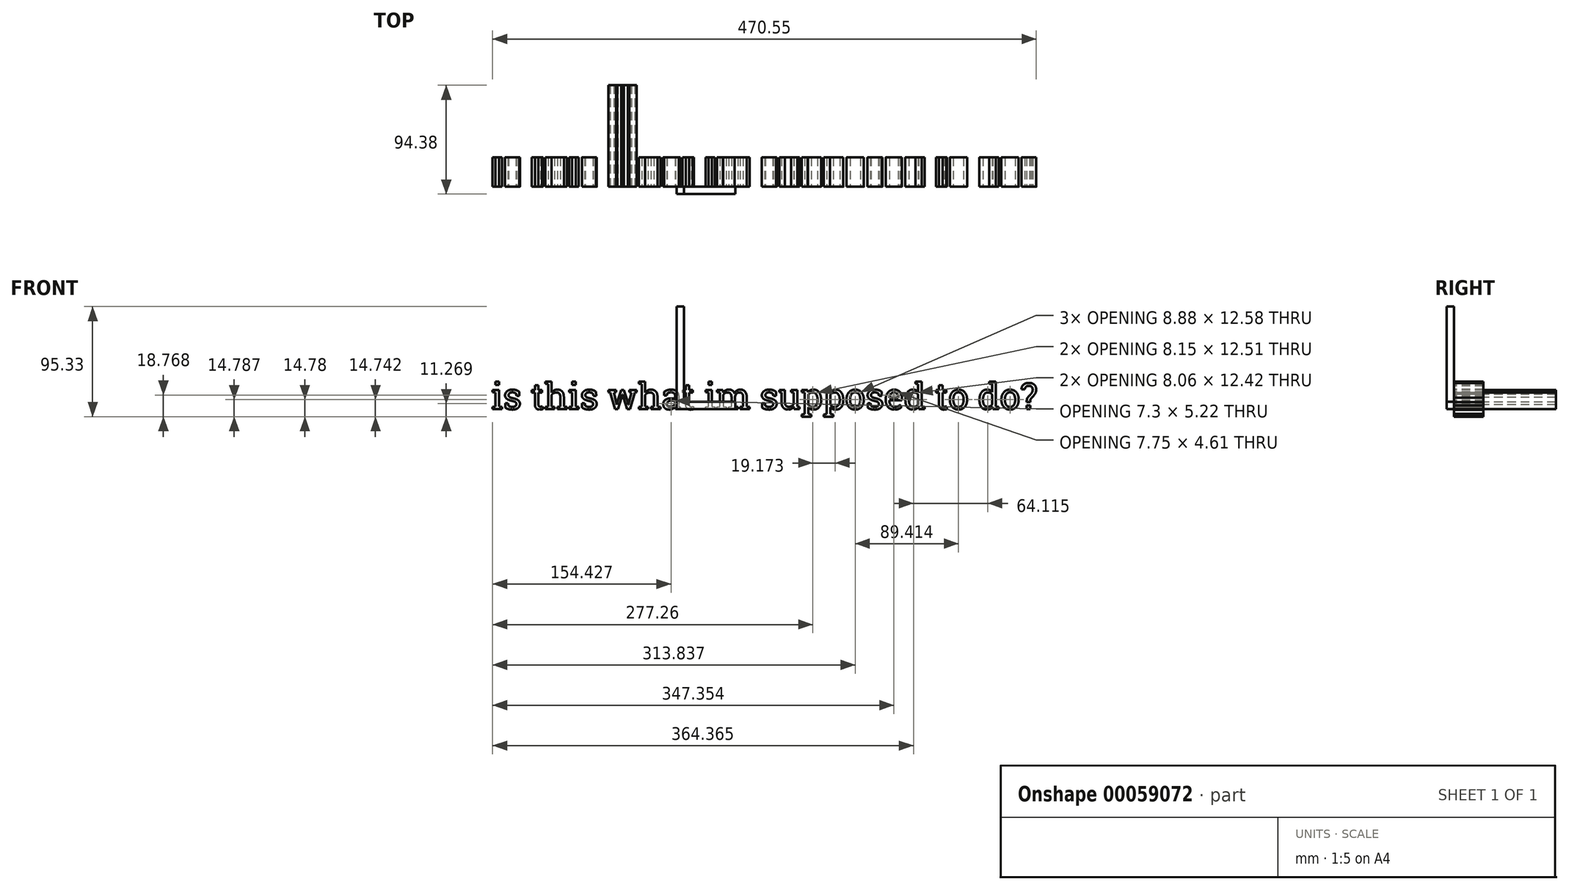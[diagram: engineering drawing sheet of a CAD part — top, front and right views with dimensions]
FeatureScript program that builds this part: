
annotation { "Feature Type Name" : "Feature", "Feature Type Description" : "" }
export const myFeature = defineFeature(function(context is Context, id is Id, definition is map)
    precondition{}
    {
        {
            var Q0;
            Q0=qCreatedBy(makeId("Front.planeOp"),FACE);
            var sketch = newSketch(context, id + "F0", { "sketchPlane" : qUnion([Q0])});
            skLineSegment(sketch, "E0", {"start": v(0, 88.9) * mm, "end": v(0, 0) * mm});
            skLineSegment(sketch, "E1", {"start": v(0, 0) * mm, "end": v(50.8, 0) * mm});
            skLineSegment(sketch, "E2", {"start": v(50.8, 0) * mm, "end": v(50.8, 6.35) * mm});
            skLineSegment(sketch, "E3", {"start": v(50.8, 6.35) * mm, "end": v(6.35, 6.35) * mm});
            skLineSegment(sketch, "E4", {"start": v(6.35, 6.35) * mm, "end": v(6.35, 88.9) * mm});
            skLineSegment(sketch, "E5", {"start": v(6.35, 88.9) * mm, "end": v(0, 88.9) * mm});
            skSolve(sketch);
        }
        {
            var Q0;
            Q0=makeQuery(id+"F0.imprint","IMPRINT",FACE,{"disambiguationData":[TD([[makeQuery(id+"F0.imprint","IMPRINT",EDGE,{"derivedFrom":sQuery(id+"F0.wireOp",EDGE,"E0")}),1.0]])]});
            extrude(context, id + "F1", {"entities" : qUnion([Q0]), "depth" : 6.35 * mm});
        }
        {
            var Q0;
            Q0=qCreatedBy(makeId("Front.planeOp"),FACE);
            var sketch = newSketch(context, id + "F2", { "sketchPlane" : qUnion([Q0])});
            skText(sketch, "E6", { "text": "is this what im supposed to do?", "fontName": "RobotoSlab-Regular.ttf"});
            const initialGuessF2  = {"E6": [-0.16075, 0, 1, 0, 0.0228]};
            skSetInitialGuess(sketch, initialGuessF2);
            skSolve(sketch);
        }
        {
            var Q0;
            Q0=makeQuery(id+"F2.imprint","IMPRINT",FACE,{"disambiguationData":[TD([[makeQuery(id+"F2.imprint","IMPRINT",EDGE,{"derivedFrom":sQuery(id+"F2.wireOp",EDGE,"E6.sketch_text.stroke-134")}),-1.0]])]});
            extrude(context, id + "F3", {"entities" : qUnion([Q0]), "oppositeDirection" : true, "depth" : 88.03 * mm});
        }
        {
            var Q0;
            Q0=makeQuery(id+"F2.imprint","IMPRINT",FACE,{"disambiguationData":[TD([[makeQuery(id+"F2.imprint","IMPRINT",EDGE,{"derivedFrom":sQuery(id+"F2.wireOp",EDGE,"E6.sketch_text.stroke-0")}),-1.0]])]});
            var Q1;
            Q1=makeQuery(id+"F2.imprint","IMPRINT",FACE,{"disambiguationData":[TD([[makeQuery(id+"F2.imprint","IMPRINT",EDGE,{"derivedFrom":sQuery(id+"F2.wireOp",EDGE,"E6.sketch_text.stroke-14")}),-1.0]])]});
            var Q2;
            Q2=makeQuery(id+"F2.imprint","IMPRINT",FACE,{"disambiguationData":[TD([[makeQuery(id+"F2.imprint","IMPRINT",EDGE,{"derivedFrom":sQuery(id+"F2.wireOp",EDGE,"E6.sketch_text.stroke-44")}),-1.0]])]});
            var Q3;
            Q3=makeQuery(id+"F2.imprint","IMPRINT",FACE,{"disambiguationData":[TD([[makeQuery(id+"F2.imprint","IMPRINT",EDGE,{"derivedFrom":sQuery(id+"F2.wireOp",EDGE,"E6.sketch_text.stroke-64")}),-1.0]])]});
            var Q4;
            Q4=makeQuery(id+"F2.imprint","IMPRINT",FACE,{"disambiguationData":[TD([[makeQuery(id+"F2.imprint","IMPRINT",EDGE,{"derivedFrom":sQuery(id+"F2.wireOp",EDGE,"E6.sketch_text.stroke-90")}),-1.0]])]});
            var Q5;
            Q5=makeQuery(id+"F2.imprint","IMPRINT",FACE,{"disambiguationData":[TD([[makeQuery(id+"F2.imprint","IMPRINT",EDGE,{"derivedFrom":sQuery(id+"F2.wireOp",EDGE,"E6.sketch_text.stroke-104")}),-1.0]])]});
            var Q6;
            Q6=makeQuery(id+"F2.imprint","IMPRINT",FACE,{"disambiguationData":[TD([[makeQuery(id+"F2.imprint","IMPRINT",EDGE,{"derivedFrom":sQuery(id+"F2.wireOp",EDGE,"E6.sketch_text.stroke-10")}),-1.0]])]});
            var Q7;
            Q7=makeQuery(id+"F2.imprint","IMPRINT",FACE,{"disambiguationData":[TD([[makeQuery(id+"F2.imprint","IMPRINT",EDGE,{"derivedFrom":sQuery(id+"F2.wireOp",EDGE,"E6.sketch_text.stroke-100")}),-1.0]])]});
            var Q8;
            Q8=makeQuery(id+"F2.imprint","IMPRINT",FACE,{"disambiguationData":[TD([[makeQuery(id+"F2.imprint","IMPRINT",EDGE,{"derivedFrom":sQuery(id+"F2.wireOp",EDGE,"E6.sketch_text.stroke-164")}),-1.0]])]});
            var Q9;
            Q9=makeQuery(id+"F2.imprint","IMPRINT",FACE,{"disambiguationData":[TD([[makeQuery(id+"F2.imprint","IMPRINT",EDGE,{"derivedFrom":sQuery(id+"F2.wireOp",EDGE,"E6.sketch_text.stroke-190")}),-1.0]])]});
            extrude(context, id + "F4", {"entities" : qUnion([Q0, Q1, Q2, Q3, Q4, Q5, Q6, Q7, Q8, Q9]), "operationType" : NewBodyOperationType.ADD, "oppositeDirection" : true, "depth" : 25.4 * mm});
        }
        {
            var Q0;
            Q0=makeQuery(id+"F2.imprint","IMPRINT",FACE,{"disambiguationData":[TD([[makeQuery(id+"F2.imprint","IMPRINT",EDGE,{"derivedFrom":sQuery(id+"F2.wireOp",EDGE,"E6.sketch_text.stroke-225")}),-1.0]])]});
            var Q1;
            Q1=makeQuery(id+"F2.imprint","IMPRINT",FACE,{"disambiguationData":[TD([[makeQuery(id+"F2.imprint","IMPRINT",EDGE,{"derivedFrom":sQuery(id+"F2.wireOp",EDGE,"E6.sketch_text.stroke-245")}),-1.0]])]});
            var Q2;
            Q2=makeQuery(id+"F2.imprint","IMPRINT",FACE,{"disambiguationData":[TD([[makeQuery(id+"F2.imprint","IMPRINT",EDGE,{"derivedFrom":sQuery(id+"F2.wireOp",EDGE,"E6.sketch_text.stroke-259")}),-1.0]])]});
            var Q3;
            Q3=makeQuery(id+"F2.imprint","IMPRINT",FACE,{"disambiguationData":[TD([[makeQuery(id+"F2.imprint","IMPRINT",EDGE,{"derivedFrom":sQuery(id+"F2.wireOp",EDGE,"E6.sketch_text.stroke-300")}),-1.0]])]});
            var Q4;
            Q4=makeQuery(id+"F2.imprint","IMPRINT",FACE,{"disambiguationData":[TD([[makeQuery(id+"F2.imprint","IMPRINT",EDGE,{"derivedFrom":sQuery(id+"F2.wireOp",EDGE,"E6.sketch_text.stroke-330")}),-1.0]])]});
            var Q5;
            Q5=makeQuery(id+"F2.imprint","IMPRINT",FACE,{"disambiguationData":[TD([[makeQuery(id+"F2.imprint","IMPRINT",EDGE,{"derivedFrom":sQuery(id+"F2.wireOp",EDGE,"E6.sketch_text.stroke-354")}),-1.0]])]});
            var Q6;
            Q6=makeQuery(id+"F2.imprint","IMPRINT",FACE,{"disambiguationData":[TD([[makeQuery(id+"F2.imprint","IMPRINT",EDGE,{"derivedFrom":sQuery(id+"F2.wireOp",EDGE,"E6.sketch_text.stroke-384")}),-1.0]])]});
            var Q7;
            Q7=makeQuery(id+"F2.imprint","IMPRINT",FACE,{"disambiguationData":[TD([[makeQuery(id+"F2.imprint","IMPRINT",EDGE,{"derivedFrom":sQuery(id+"F2.wireOp",EDGE,"E6.sketch_text.stroke-414")}),-1.0]])]});
            var Q8;
            Q8=makeQuery(id+"F2.imprint","IMPRINT",FACE,{"disambiguationData":[TD([[makeQuery(id+"F2.imprint","IMPRINT",EDGE,{"derivedFrom":sQuery(id+"F2.wireOp",EDGE,"E6.sketch_text.stroke-434")}),-1.0]])]});
            var Q9;
            Q9=makeQuery(id+"F2.imprint","IMPRINT",FACE,{"disambiguationData":[TD([[makeQuery(id+"F2.imprint","IMPRINT",EDGE,{"derivedFrom":sQuery(id+"F2.wireOp",EDGE,"E6.sketch_text.stroke-464")}),-1.0]])]});
            var Q10;
            Q10=makeQuery(id+"F2.imprint","IMPRINT",FACE,{"disambiguationData":[TD([[makeQuery(id+"F2.imprint","IMPRINT",EDGE,{"derivedFrom":sQuery(id+"F2.wireOp",EDGE,"E6.sketch_text.stroke-488")}),-1.0]])]});
            var Q11;
            Q11=makeQuery(id+"F2.imprint","IMPRINT",FACE,{"disambiguationData":[TD([[makeQuery(id+"F2.imprint","IMPRINT",EDGE,{"derivedFrom":sQuery(id+"F2.wireOp",EDGE,"E6.sketch_text.stroke-517")}),-1.0]])]});
            var Q12;
            Q12=makeQuery(id+"F2.imprint","IMPRINT",FACE,{"disambiguationData":[TD([[makeQuery(id+"F2.imprint","IMPRINT",EDGE,{"derivedFrom":sQuery(id+"F2.wireOp",EDGE,"E6.sketch_text.stroke-537")}),-1.0]])]});
            var Q13;
            Q13=makeQuery(id+"F2.imprint","IMPRINT",FACE,{"disambiguationData":[TD([[makeQuery(id+"F2.imprint","IMPRINT",EDGE,{"derivedFrom":sQuery(id+"F2.wireOp",EDGE,"E6.sketch_text.stroke-557")}),-1.0]])]});
            var Q14;
            Q14=makeQuery(id+"F2.imprint","IMPRINT",FACE,{"disambiguationData":[TD([[makeQuery(id+"F2.imprint","IMPRINT",EDGE,{"derivedFrom":sQuery(id+"F2.wireOp",EDGE,"E6.sketch_text.stroke-586")}),-1.0]])]});
            var Q15;
            Q15=makeQuery(id+"F2.imprint","IMPRINT",FACE,{"disambiguationData":[TD([[makeQuery(id+"F2.imprint","IMPRINT",EDGE,{"derivedFrom":sQuery(id+"F2.wireOp",EDGE,"E6.sketch_text.stroke-606")}),-1.0]])]});
            var Q16;
            Q16=makeQuery(id+"F2.imprint","IMPRINT",FACE,{"disambiguationData":[TD([[makeQuery(id+"F2.imprint","IMPRINT",EDGE,{"derivedFrom":sQuery(id+"F2.wireOp",EDGE,"E6.sketch_text.stroke-625")}),-1.0]])]});
            var Q17;
            Q17=makeQuery(id+"F2.imprint","IMPRINT",FACE,{"disambiguationData":[TD([[makeQuery(id+"F2.imprint","IMPRINT",EDGE,{"derivedFrom":sQuery(id+"F2.wireOp",EDGE,"E6.sketch_text.stroke-255")}),-1.0]])]});
            extrude(context, id + "F5", {"entities" : qUnion([Q0, Q1, Q2, Q3, Q4, Q5, Q6, Q7, Q8, Q9, Q10, Q11, Q12, Q13, Q14, Q15, Q16, Q17]), "operationType" : NewBodyOperationType.ADD, "oppositeDirection" : true, "depth" : 25.4 * mm});
        }
    });
